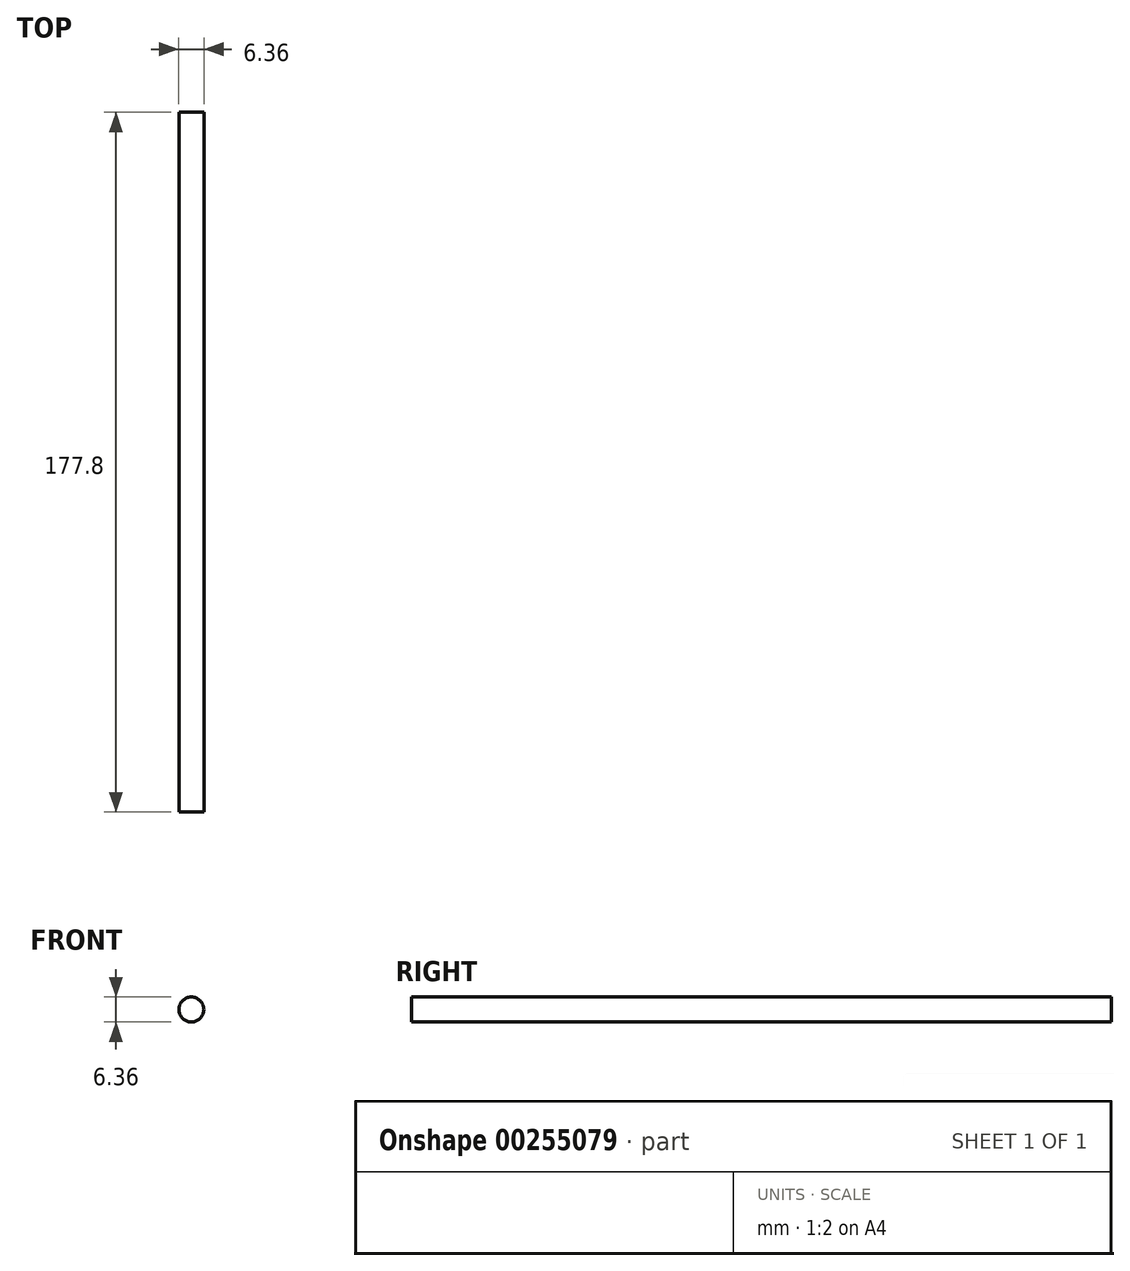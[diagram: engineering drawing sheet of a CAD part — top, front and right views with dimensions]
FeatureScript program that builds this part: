
annotation { "Feature Type Name" : "Feature", "Feature Type Description" : "" }
export const myFeature = defineFeature(function(context is Context, id is Id, definition is map)
    precondition{}
    {
        {
            var Q0;
            Q0=qCreatedBy(makeId("Front.planeOp"),FACE);
            var sketch = newSketch(context, id + "F0", { "sketchPlane" : qUnion([Q0])});
            skCircle(sketch, "E0", {"center": v(0, 0) * mm, "radius": 3.18 * mm});
            skSolve(sketch);
        }
        {
            var Q0;
            Q0 = qSketchRegion(id + "F0", true);
            extrude(context, id + "F1", {"entities" : qUnion([Q0]), "depth" : 177.8 * mm});
        }
    });
